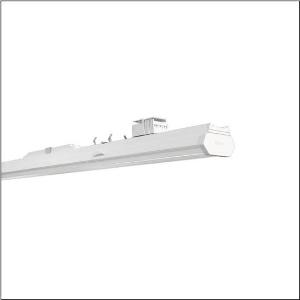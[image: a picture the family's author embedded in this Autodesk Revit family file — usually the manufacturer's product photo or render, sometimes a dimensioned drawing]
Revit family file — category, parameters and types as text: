
# Revit family: licross_r__11_protected_mo_51td12dn495g_4259
name_source: partatom
category: Lighting Fixtures
units: mm (PartAtom-declared; Revit-internal decimal feet)

## family parameters
Cut with Voids When Loaded = No
Host = Face
Light Source = No
Part Type = Normal
Room Calculation Point = No
Round Connector Dimension = Use Diameter
Shared = No

## types (1)
- --- (1 x LED, 9980 lm, 57.1 W, 4000K)
    Apparent Load = 57 VA
    CIE Flux Codes = 73 92 98 99 100
    Color Rendering = 80
    Color Temperature = 4000K
    Default Elevation = 1800 mm
    Description = Licross® 11 Protected MO, luminaire insert, of sheet steel, galvanised, coil coated, white, length: 1.500mm, width: 90mm, height: 101mm, LED rated luminous flux: 9.980lm, light colour: 840, control gear: DALI 2, with plug, 5-pole, with phase selection, mains connection: 220..240V, AC, 50/60Hz, rated input power: 57W, halogen-free wiring, primary optical cover: cover, of PMMA, light emission: direct distribution, primary light characteristic: symmetric, protection rating (complete): IP54, insulation class (complete): insulation class I (protective earthing), certification: CE, ENEC, VDE, UKCA, protection symbol: D if used in an environment with non-conductive dust loads with corresponding accessories, impact resistance: IK06, permissible ambient temperature for indoor applications: -25..+35°C, corresponds to IFS (International Featured Standards) requirements for safety and quality in the food industry, reducing of maximum allowable ambient temperature of 5°C with ceiling mounting, LABS conformity tested according to VDMA 24364:2018-05, packaging unit: 1 piece
    Height = 92 mm
    Lamp = 1 x LED
    Lamp Light Flux = 9980 lm
    Lamp Power = 57.1 W
    Lamp count = 1
    Length = 1500 mm
    Luminous efficacy = 175 lm/W
    Manufacturer = Siteco
    ModVariant = No
    Model = 51TD12DN495G
    Mounting Place = Ceiling
    Mounting Type = Pendant
    Number of Poles = 1
    OnlyDefault = Yes
    Power Factor = 1
    Product Name = Licross® 11 Protected MO
    Product group = luminaire insert
    ProductGroupID = 901
    Protection Class = Protection class I
    Protection Degree = IP 54
    RLX_Detail_Level = 1
    RLX_Emergency_Light_Flux = 0 lm
    RLX_Emergency_Type = 0
    RLX_Emergency_Type_DB = No
    RlxData = <blob elided: 24469 chars, md5=37d8fe95>
    Socket = socket
    Standby Power = 0 W
    System Light Flux = 9980 lm
    System Power = 57 W
    Type Comments = factory setting: luminous flux: 100 % | dim-lin: 254 | 378 mA
    Type Image = l_1256145.jpg
    URL = http://relux.com
    VarID = @adj_049425
    Voltage = 0 V
    Weight = 0.00 kg
    Width = 88 mm

## geometry (parser evidence)
native form markers: Blend x4, Sweep x11
no freeform markers — native parametric forms only
